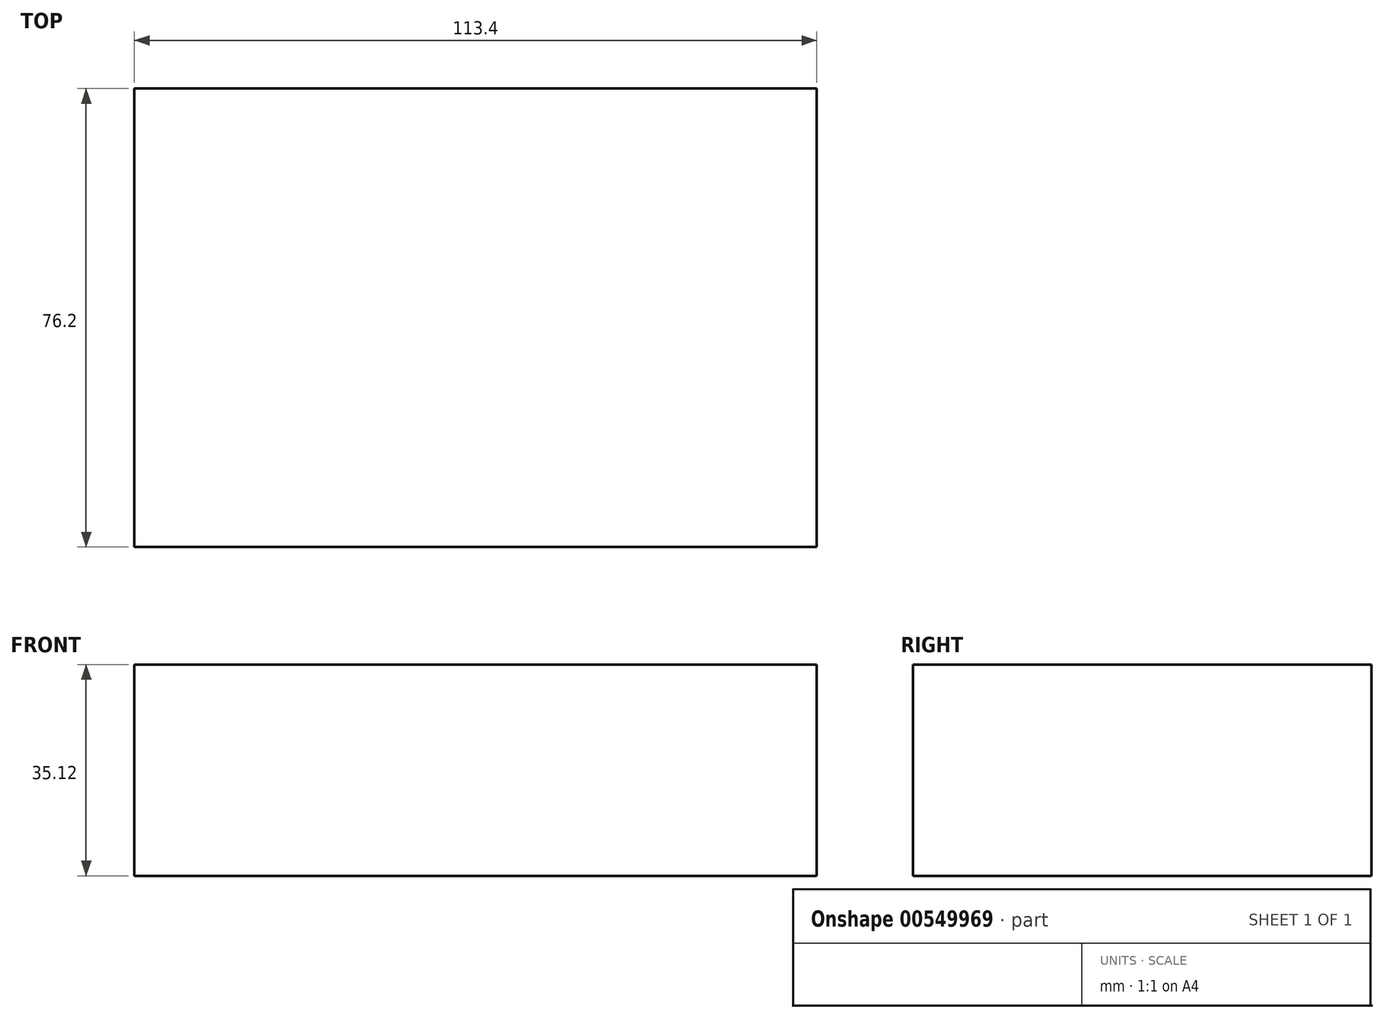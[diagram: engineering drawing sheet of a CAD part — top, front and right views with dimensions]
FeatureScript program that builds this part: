
annotation { "Feature Type Name" : "Feature", "Feature Type Description" : "" }
export const myFeature = defineFeature(function(context is Context, id is Id, definition is map)
    precondition{}
    {
        {
            var Q0;
            Q0=qCreatedBy(makeId("Front.planeOp"),FACE);
            var sketch = newSketch(context, id + "F0", { "sketchPlane" : qUnion([Q0])});
            skLineSegment(sketch, "E0.bottom", {"start": v(-56.7, 17.56) * mm, "end": v(56.7, 17.56) * mm});
            skLineSegment(sketch, "E0.top", {"start": v(-56.7, -17.56) * mm, "end": v(56.7, -17.56) * mm});
            skLineSegment(sketch, "E0.left", {"start": v(-56.7, 17.56) * mm, "end": v(-56.7, -17.56) * mm});
            skLineSegment(sketch, "E0.right", {"start": v(56.7, 17.56) * mm, "end": v(56.7, -17.56) * mm});
            skPoint(sketch, "E0.middle", {"position": v(0, 0) * mm});
            skSolve(sketch);
        }
        {
            var Q0;
            Q0=makeQuery(id+"F0.imprint","IMPRINT",FACE,{"disambiguationData":[TD([[makeQuery(id+"F0.imprint","IMPRINT",EDGE,{"derivedFrom":sQuery(id+"F0.wireOp",EDGE,"E0.bottom")}),-1.0]])]});
            extrude(context, id + "F1", {"entities" : qUnion([Q0]), "endBound" : BoundingType.SYMMETRIC, "depth" : 76.2 * mm, "offsetDistance" : 25.4 * mm});
        }
    });
